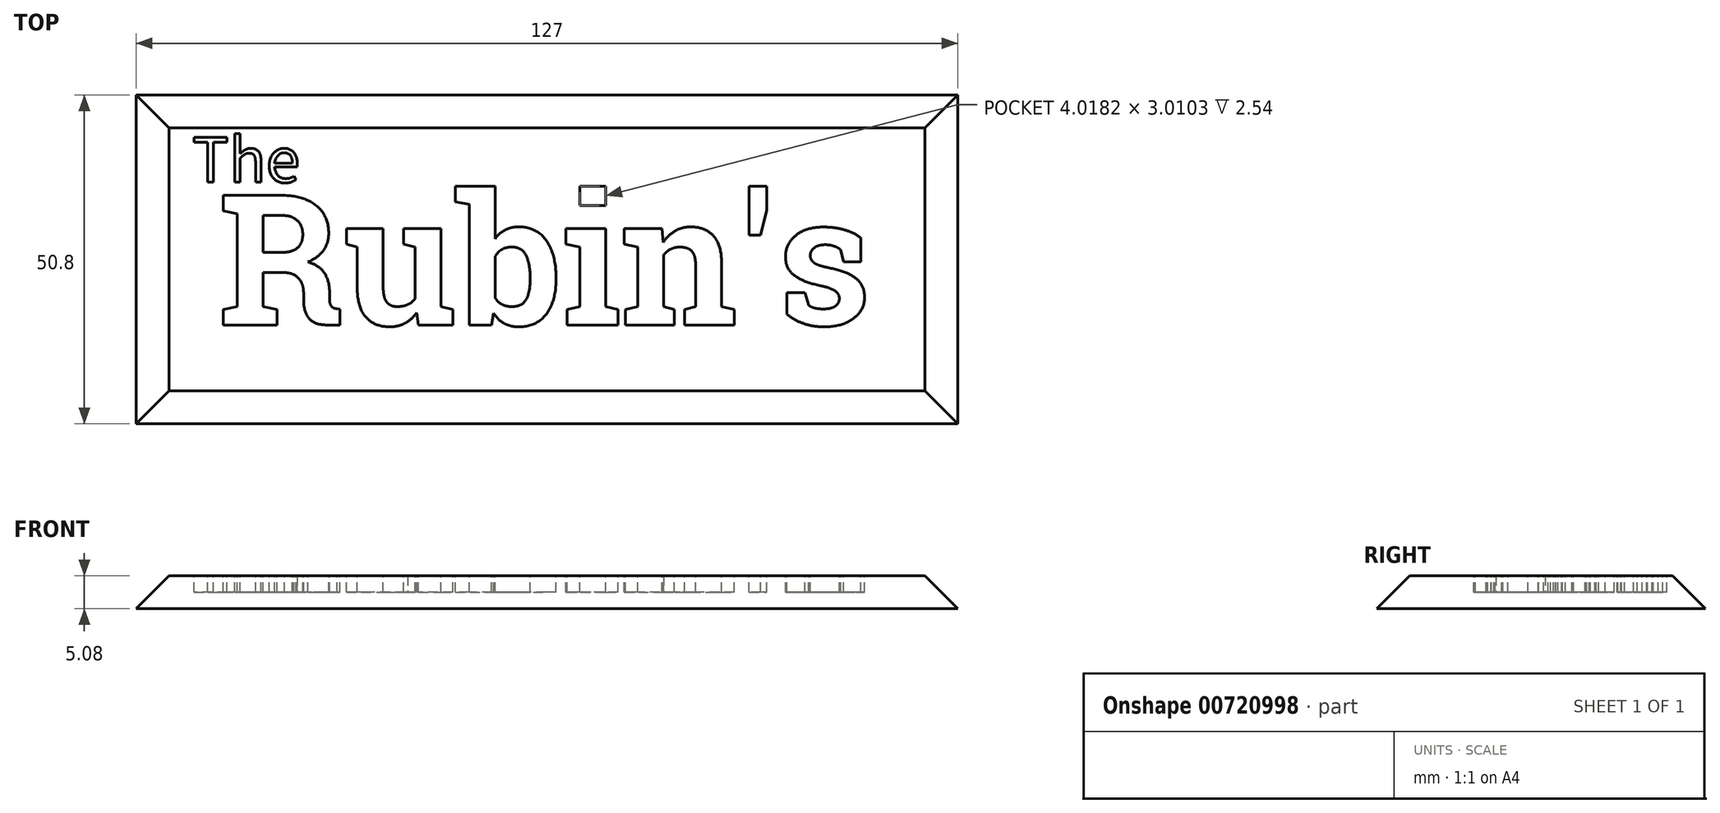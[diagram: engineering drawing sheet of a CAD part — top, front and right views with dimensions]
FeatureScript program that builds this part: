
annotation { "Feature Type Name" : "Feature", "Feature Type Description" : "" }
export const myFeature = defineFeature(function(context is Context, id is Id, definition is map)
    precondition{}
    {
        {
            var Q0;
            Q0=qCreatedBy(makeId("Top.planeOp"),FACE);
            var sketch = newSketch(context, id + "F0", { "sketchPlane" : qUnion([Q0])});
            skLineSegment(sketch, "E0.bottom", {"start": v(63.5, 25.4) * mm, "end": v(-63.5, 25.4) * mm});
            skLineSegment(sketch, "E0.top", {"start": v(63.5, -25.4) * mm, "end": v(-63.5, -25.4) * mm});
            skLineSegment(sketch, "E0.left", {"start": v(63.5, 25.4) * mm, "end": v(63.5, -25.4) * mm});
            skLineSegment(sketch, "E0.right", {"start": v(-63.5, 25.4) * mm, "end": v(-63.5, -25.4) * mm});
            skPoint(sketch, "E0.middle", {"position": v(0, 0) * mm});
            skSolve(sketch);
        }
        {
            var Q0;
            Q0=makeQuery(id+"F0.imprint","IMPRINT",FACE,{"disambiguationData":[TD([[makeQuery(id+"F0.imprint","IMPRINT",EDGE,{"derivedFrom":sQuery(id+"F0.wireOp",EDGE,"E0.bottom")}),1.0]])]});
            extrude(context, id + "F1", {"entities" : qUnion([Q0]), "depth" : 5.08 * mm, "offsetDistance" : 25.4 * mm});
        }
        {
            var Q0;
            Q0=makeQuery(id+"F1.opExtrude","CAP_EDGE",EDGE,{"disambiguationData":[OSD([sQuery(id+"F0.wireOp",EDGE,"E0.top")])],"isStart":false});
            var Q1;
            Q1=makeQuery(id+"F1.opExtrude","CAP_EDGE",EDGE,{"disambiguationData":[OSD([sQuery(id+"F0.wireOp",EDGE,"E0.right")])],"isStart":false});
            var Q2;
            Q2=makeQuery(id+"F1.opExtrude","CAP_EDGE",EDGE,{"disambiguationData":[OSD([sQuery(id+"F0.wireOp",EDGE,"E0.bottom")])],"isStart":false});
            var Q3;
            Q3=makeQuery(id+"F1.opExtrude","CAP_EDGE",EDGE,{"disambiguationData":[OSD([sQuery(id+"F0.wireOp",EDGE,"E0.left")])],"isStart":false});
            chamfer(context, id + "F2", {"entities" : qUnion([Q0, Q1, Q2, Q3]), "width" : 5.08 * mm, "tangentPropagation" : true});
        }
        {
            var Q0;
            Q0=makeQuery(id+"F1.opExtrude","CAP_FACE",FACE,{"disambiguationData":[OSD([sQuery(id+"F0.wireOp",EDGE,"E0.bottom"),sQuery(id+"F0.wireOp",EDGE,"E0.top"),sQuery(id+"F0.wireOp",EDGE,"E0.left"),sQuery(id+"F0.wireOp",EDGE,"E0.right")])],"isStart":false});
            var sketch = newSketch(context, id + "F3", { "sketchPlane" : qUnion([Q0])});
            skText(sketch, "E1", { "text": "Rubin\'s", "fontName": "RobotoSlab-Bold.ttf"});
            skPoint(sketch, "E2", {"position": v(0, 0) * mm});
            skText(sketch, "E3", { "text": "The", "fontName": "NotoSansCJKkr-Regular.otf"});
            const initialGuessF3  = {"E1": [-0.0508, -0.01014, 1, 0, 0.02028], "E3": [-0.05482, 0.0119, 1, 0, 0.0068]};
            skSetInitialGuess(sketch, initialGuessF3);
            skSolve(sketch);
        }
        {
            var Q0;
            Q0 = qSketchRegion(id + "F3", true);
            extrude(context, id + "F4", {"entities" : qUnion([Q0]), "operationType" : NewBodyOperationType.REMOVE, "oppositeDirection" : true, "depth" : 2.54 * mm, "offsetDistance" : 25.4 * mm});
        }
    });
